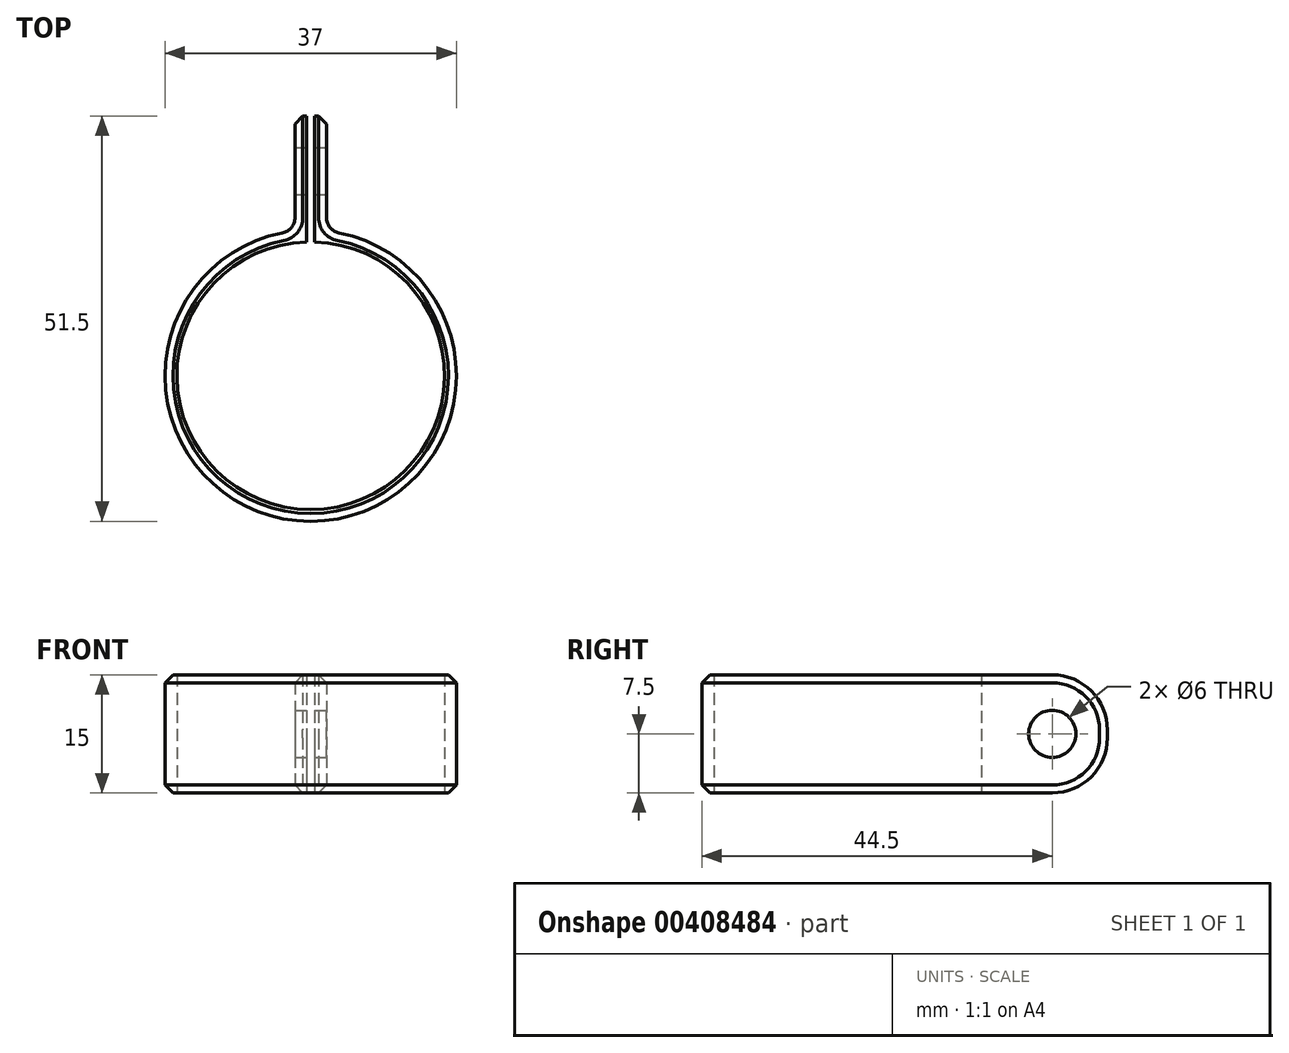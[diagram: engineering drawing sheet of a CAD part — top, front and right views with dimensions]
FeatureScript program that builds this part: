
annotation { "Feature Type Name" : "Feature", "Feature Type Description" : "" }
export const myFeature = defineFeature(function(context is Context, id is Id, definition is map)
    precondition{}
    {
        {
            var Q0;
            Q0=qCreatedBy(makeId("Top.planeOp"),FACE);
            var sketch = newSketch(context, id + "F0", { "sketchPlane" : qUnion([Q0])});
            skArc(sketch, "E0", {"start": v(-3.6, 18.14) * mm, "mid": v(0, -18.5) * mm, "end": v(3.6, 18.14) * mm});
            skLineSegment(sketch, "E1", {"start": v(-2, 20.1) * mm, "end": v(-2, 33) * mm});
            skLineSegment(sketch, "E2", {"start": v(2, 20.1) * mm, "end": v(2, 33) * mm});
            skPoint(sketch, "E3.visualSharp", {"position": v(2, 18.4) * mm});
            skArc(sketch, "E3.filletArc", {"start": v(2, 20.1) * mm, "mid": v(2.45, 18.84) * mm, "end": v(3.6, 18.14) * mm});
            skPoint(sketch, "E4.visualSharp", {"position": v(-2, 18.4) * mm});
            skArc(sketch, "E4.filletArc", {"start": v(-3.6, 18.14) * mm, "mid": v(-2.45, 18.84) * mm, "end": v(-2, 20.1) * mm});
            skLineSegment(sketch, "E5.0", {"start": v(0.5, 17) * mm, "end": v(0.5, 33) * mm});
            skArc(sketch, "E6.0", {"start": v(-0.5, 17) * mm, "mid": v(0, -17) * mm, "end": v(0.5, 17) * mm});
            skLineSegment(sketch, "E7.0", {"start": v(-0.5, 17) * mm, "end": v(-0.5, 33) * mm});
            skLineSegment(sketch, "E8", {"start": v(0.5, 33) * mm, "end": v(2, 33) * mm});
            skLineSegment(sketch, "E9", {"start": v(-0.5, 33) * mm, "end": v(-2, 33) * mm});
            skSolve(sketch);
        }
        {
            var Q0;
            Q0 = qSketchRegion(id + "F0", true);
            extrude(context, id + "F1", {"entities" : qUnion([Q0]), "depth" : 15 * mm});
        }
        {
            var Q0;
            Q0=makeQuery(id+"F1.opExtrude","CAP_EDGE",EDGE,{"disambiguationData":[OSD([sQuery(id+"F0.wireOp",EDGE,"E8")])],"isStart":false});
            var Q1;
            Q1=makeQuery(id+"F1.opExtrude","CAP_EDGE",EDGE,{"disambiguationData":[OSD([sQuery(id+"F0.wireOp",EDGE,"E9")])],"isStart":false});
            var Q2;
            Q2=makeQuery(id+"F1.opExtrude","CAP_EDGE",EDGE,{"disambiguationData":[OSD([sQuery(id+"F0.wireOp",EDGE,"E8")])],"isStart":true});
            var Q3;
            Q3=makeQuery(id+"F1.opExtrude","CAP_EDGE",EDGE,{"disambiguationData":[OSD([sQuery(id+"F0.wireOp",EDGE,"E9")])],"isStart":true});
            fillet(context, id + "F2", {"entities" : qUnion([Q0, Q1, Q2, Q3]), "radius" : 7 * mm, "tangentPropagation" : true, "allowEdgeOverflow" : false});
        }
        {
            var Q0;
            Q0=makeQuery(id+"F1.opExtrude","SWEPT_FACE",FACE,{"disambiguationData":[OSD([sQuery(id+"F0.wireOp",EDGE,"E2")])]});
            var sketch = newSketch(context, id + "F3", { "sketchPlane" : qUnion([Q0])});
            skCircle(sketch, "E10", {"center": v(26, 7.5) * mm, "radius": 3 * mm});
            skPoint(sketch, "E10.centerSnap0", {"position": v(33, 7.5) * mm});
            skSolve(sketch);
        }
        {
            var Q0;
            Q0=makeQuery(id+"F3.imprint","IMPRINT",FACE,{"disambiguationData":[TD([[makeQuery(id+"F3.imprint","IMPRINT",EDGE,{"derivedFrom":sQuery(id+"F3.wireOp",EDGE,"E10")}),1.0]])]});
            extrude(context, id + "F4", {"entities" : qUnion([Q0]), "operationType" : NewBodyOperationType.REMOVE, "oppositeDirection" : true, "depth" : 25 * mm});
        }
        {
            var Q0;
            Q0=makeQuery(id+"F1.opExtrude","CAP_EDGE",EDGE,{"disambiguationData":[OSD([sQuery(id+"F0.wireOp",EDGE,"E2")])],"isStart":false});
            chamfer(context, id + "F5", {"entities" : qUnion([Q0]), "chamferType" : ChamferType.OFFSET_ANGLE, "width" : 1 * mm, "oppositeDirection" : false, "angle" : 45 * degree, "tangentPropagation" : true});
        }
    });
